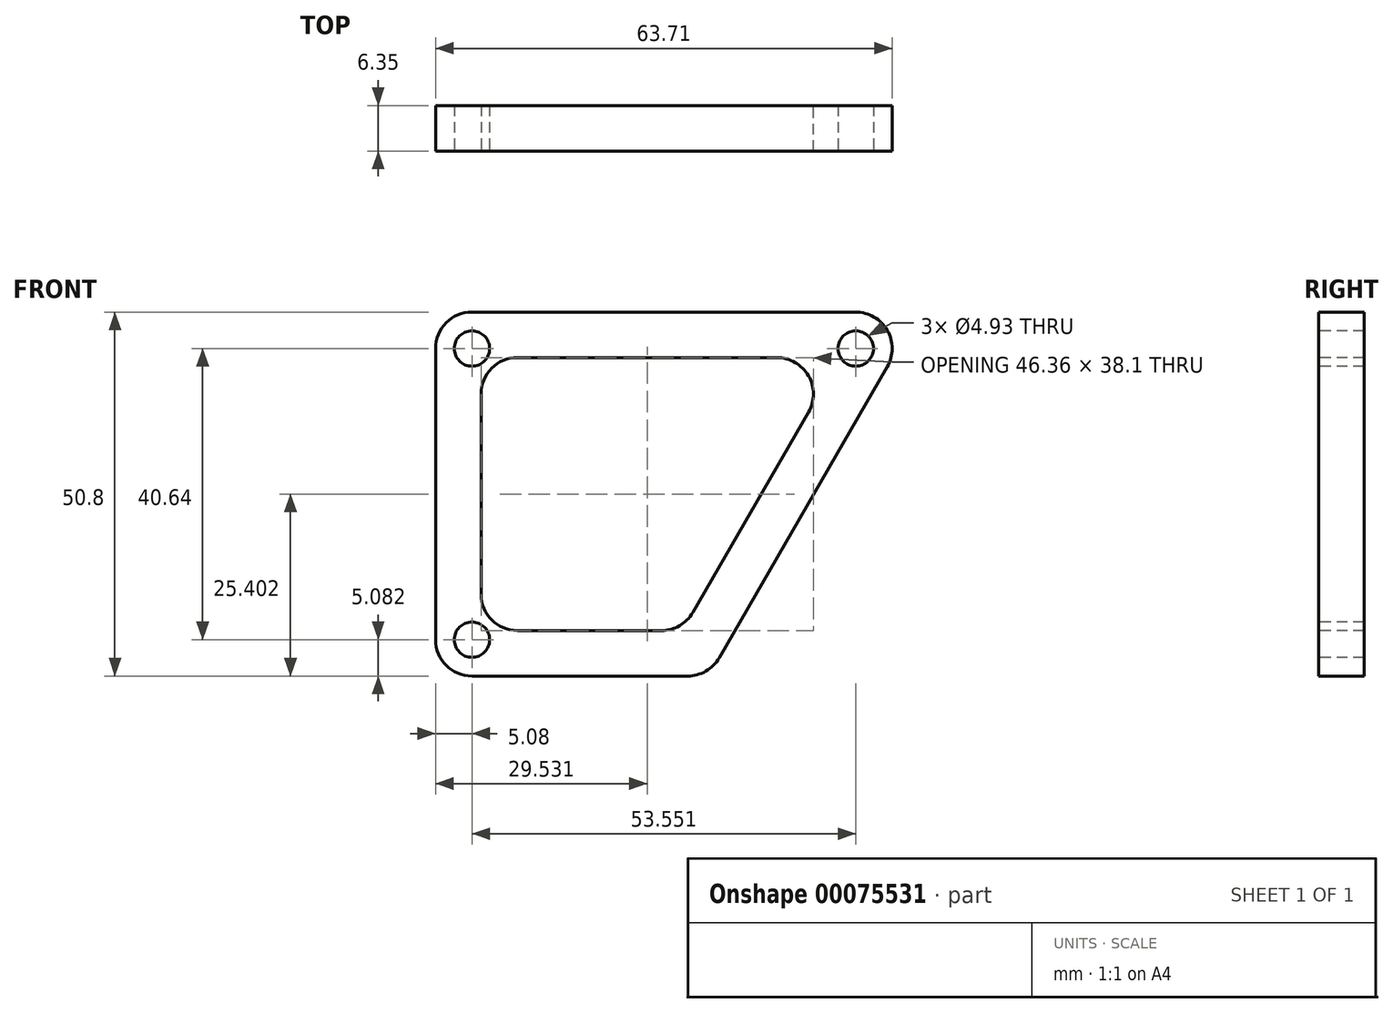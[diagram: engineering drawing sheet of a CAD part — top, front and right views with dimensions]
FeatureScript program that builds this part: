
annotation { "Feature Type Name" : "Feature", "Feature Type Description" : "" }
export const myFeature = defineFeature(function(context is Context, id is Id, definition is map)
    precondition{}
    {
        {
            var Q0;
            Q0=qCreatedBy(makeId("Front.planeOp"),FACE);
            var sketch = newSketch(context, id + "F0", { "sketchPlane" : qUnion([Q0])});
            skLineSegment(sketch, "E0", {"start": v(-75.92, 54.78) * mm, "end": v(-75.92, 3.98) * mm});
            skLineSegment(sketch, "E1", {"start": v(-75.92, 3.98) * mm, "end": v(-37.82, 3.98) * mm});
            skLineSegment(sketch, "E2", {"start": v(-37.82, 3.98) * mm, "end": v(-8.5, 54.78) * mm});
            skLineSegment(sketch, "E3", {"start": v(-8.5, 54.78) * mm, "end": v(-75.92, 54.78) * mm});
            skSolve(sketch);
        }
        {
            var Q0;
            Q0=makeQuery(id+"F0.imprint","IMPRINT",FACE,{"disambiguationData":[TD([[makeQuery(id+"F0.imprint","IMPRINT",EDGE,{"derivedFrom":sQuery(id+"F0.wireOp",EDGE,"E0")}),1.0]])]});
            extrude(context, id + "F1", {"entities" : qUnion([Q0]), "depth" : 6.35 * mm});
        }
        {
            var Q0;
            Q0=makeQuery(id+"F1.opExtrude","CAP_FACE",FACE,{"disambiguationData":[OSD([sQuery(id+"F0.wireOp",EDGE,"E0"),sQuery(id+"F0.wireOp",EDGE,"E1"),sQuery(id+"F0.wireOp",EDGE,"E2"),sQuery(id+"F0.wireOp",EDGE,"E3")])],"isStart":false});
            var sketch = newSketch(context, id + "F2", { "sketchPlane" : qUnion([Q0])});
            skLineSegment(sketch, "E4.0", {"start": v(-19.49, 48.43) * mm, "end": v(-69.57, 48.43) * mm});
            skLineSegment(sketch, "E5.0", {"start": v(-69.57, 48.43) * mm, "end": v(-69.57, 10.33) * mm});
            skLineSegment(sketch, "E6.0", {"start": v(-69.57, 10.33) * mm, "end": v(-41.49, 10.33) * mm});
            skLineSegment(sketch, "E7.0", {"start": v(-41.49, 10.33) * mm, "end": v(-19.49, 48.43) * mm});
            skSolve(sketch);
        }
        {
            var Q0;
            Q0=makeQuery(id+"F2.imprint","IMPRINT",FACE,{"disambiguationData":[TD([[makeQuery(id+"F2.imprint","IMPRINT",EDGE,{"derivedFrom":sQuery(id+"F2.wireOp",EDGE,"E4.0")}),1.0]])]});
            extrude(context, id + "F3", {"entities" : qUnion([Q0]), "operationType" : NewBodyOperationType.REMOVE, "oppositeDirection" : true, "depth" : 25.4 * mm});
        }
        {
            var Q0;
            Q0=makeQuery(id+"F1.opExtrude","SWEPT_EDGE",EDGE,{"disambiguationData":[OSD([sQuery(id+"F0.wireOp",EDGE,"E2"),sQuery(id+"F0.wireOp",EDGE,"E3")])]});
            var Q1;
            Q1=makeQuery(id+"F1.opExtrude","SWEPT_EDGE",EDGE,{"disambiguationData":[OSD([sQuery(id+"F0.wireOp",EDGE,"E0"),sQuery(id+"F0.wireOp",EDGE,"E3")])]});
            var Q2;
            Q2=makeQuery(id+"F1.opExtrude","SWEPT_EDGE",EDGE,{"disambiguationData":[OSD([sQuery(id+"F0.wireOp",EDGE,"E1"),sQuery(id+"F0.wireOp",EDGE,"E2")])]});
            var Q3;
            Q3=makeQuery(id+"F1.opExtrude","SWEPT_EDGE",EDGE,{"disambiguationData":[OSD([sQuery(id+"F0.wireOp",EDGE,"E0"),sQuery(id+"F0.wireOp",EDGE,"E1")])]});
            fillet(context, id + "F4", {"entities" : qUnion([Q0, Q1, Q2, Q3]), "radius" : 5.08 * mm, "tangentPropagation" : true, "allowEdgeOverflow" : false});
        }
        {
            var Q0;
            Q0=makeQuery(id+"F3.boolean.opBoolean","COPY",EDGE,{"derivedFrom":makeQuery(id+"F3.opExtrude","SWEPT_EDGE",EDGE,{"disambiguationData":[OSD([sQuery(id+"F2.wireOp",EDGE,"E6.0"),sQuery(id+"F2.wireOp",EDGE,"E7.0")])]})});
            var Q1;
            Q1=makeQuery(id+"F3.boolean.opBoolean","COPY",EDGE,{"derivedFrom":makeQuery(id+"F3.opExtrude","SWEPT_EDGE",EDGE,{"disambiguationData":[OSD([sQuery(id+"F2.wireOp",EDGE,"E5.0"),sQuery(id+"F2.wireOp",EDGE,"E6.0")])]})});
            var Q2;
            Q2=makeQuery(id+"F3.boolean.opBoolean","COPY",EDGE,{"derivedFrom":makeQuery(id+"F3.opExtrude","SWEPT_EDGE",EDGE,{"disambiguationData":[OSD([sQuery(id+"F2.wireOp",EDGE,"E4.0"),sQuery(id+"F2.wireOp",EDGE,"E5.0")])]})});
            var Q3;
            Q3=makeQuery(id+"F3.boolean.opBoolean","COPY",EDGE,{"derivedFrom":makeQuery(id+"F3.opExtrude","SWEPT_EDGE",EDGE,{"disambiguationData":[OSD([sQuery(id+"F2.wireOp",EDGE,"E4.0"),sQuery(id+"F2.wireOp",EDGE,"E7.0")])]})});
            fillet(context, id + "F5", {"entities" : qUnion([Q0, Q1, Q2, Q3]), "radius" : 5.08 * mm, "tangentPropagation" : true, "allowEdgeOverflow" : false});
        }
        {
            var Q0;
            Q0=makeQuery(id+"F1.opExtrude","CAP_FACE",FACE,{"disambiguationData":[OSD([sQuery(id+"F0.wireOp",EDGE,"E0"),sQuery(id+"F0.wireOp",EDGE,"E1"),sQuery(id+"F0.wireOp",EDGE,"E2"),sQuery(id+"F0.wireOp",EDGE,"E3")])],"isStart":false});
            var sketch = newSketch(context, id + "F6", { "sketchPlane" : qUnion([Q0])});
            skPoint(sketch, "E8", {"position": v(-70.84, 49.7) * mm});
            skPoint(sketch, "E9", {"position": v(-70.84, 9.06) * mm});
            skPoint(sketch, "E10", {"position": v(-17.29, 49.7) * mm});
            skSolve(sketch);
        }
        {
            var Q0;
            Q0=sQuery(id+"F6.wireOp",VERTEX,"E8");
            var Q1;
            Q1=sQuery(id+"F6.wireOp",VERTEX,"E9");
            var Q2;
            Q2=sQuery(id+"F6.wireOp",VERTEX,"E10");
            var Q3;
            Q3=makeQuery(id+"F1.opExtrude","SWEPT_BODY",BODY,{"disambiguationData":[OSD([sQuery(id+"F0.wireOp",EDGE,"E0"),sQuery(id+"F0.wireOp",EDGE,"E1"),sQuery(id+"F0.wireOp",EDGE,"E2"),sQuery(id+"F0.wireOp",EDGE,"E3")])]});
            hole(context, id + "F7", {"style" : HoleStyle.SIMPLE, "holeDiameter" : 4.93 * mm, "endStyle" : HoleEndStyle.THROUGH, "locations" : qUnion([Q0, Q1, Q2]), "scope" : qUnion([Q3])});
        }
    });
